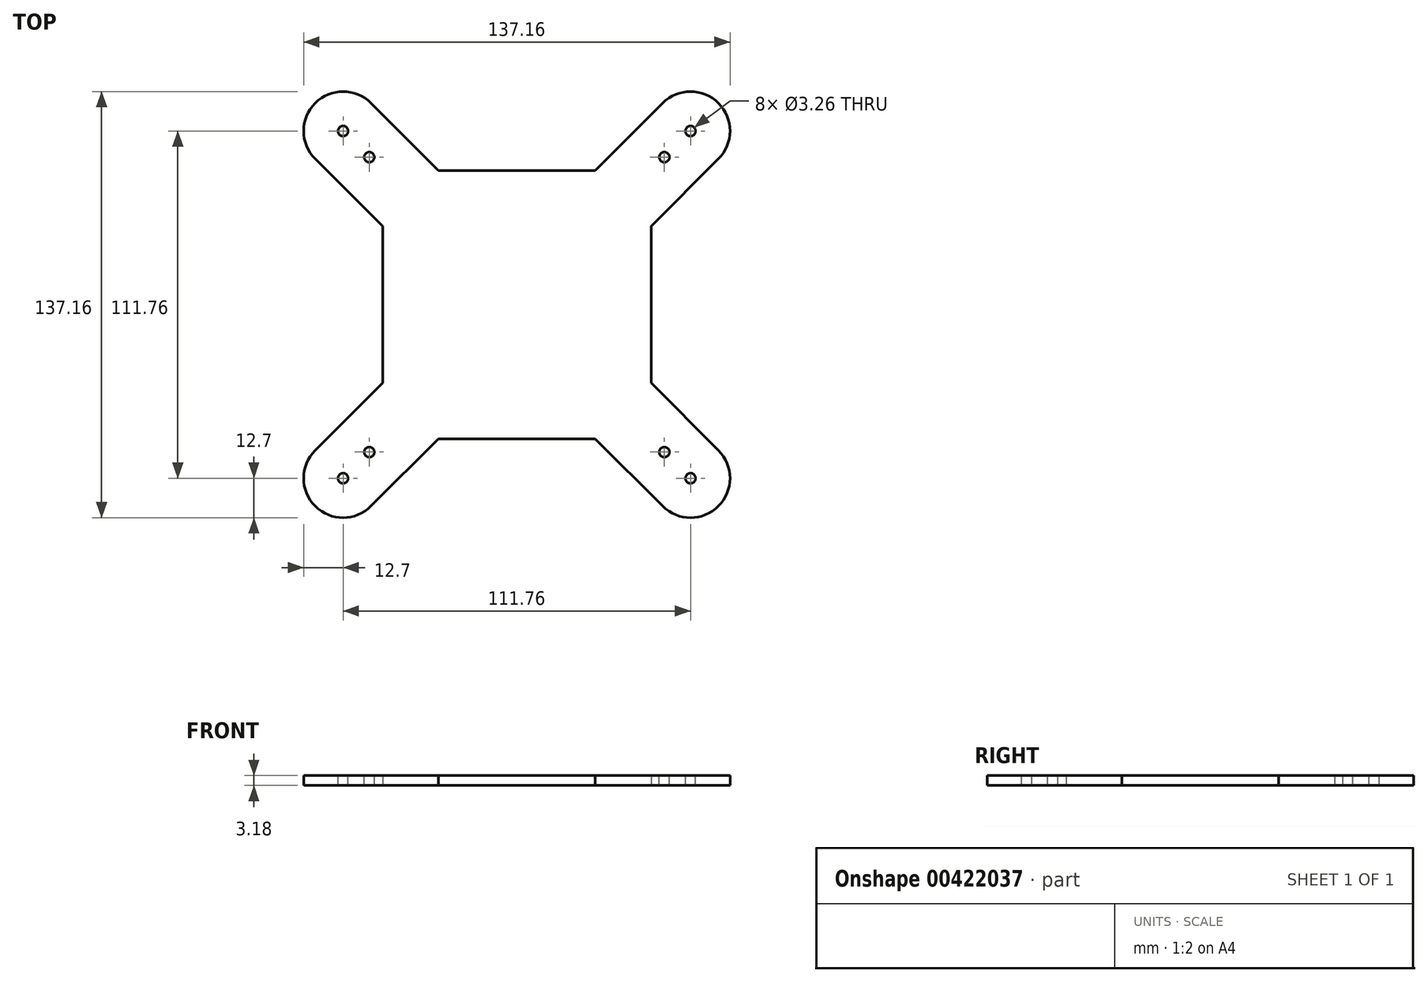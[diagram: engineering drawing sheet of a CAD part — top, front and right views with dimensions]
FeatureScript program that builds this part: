
annotation { "Feature Type Name" : "Feature", "Feature Type Description" : "" }
export const myFeature = defineFeature(function(context is Context, id is Id, definition is map)
    precondition{}
    {
        {
            var Q0;
            Q0=qCreatedBy(makeId("Top.planeOp"),FACE);
            var sketch = newSketch(context, id + "F0", { "sketchPlane" : qUnion([Q0])});
            skPoint(sketch, "E0.middle", {"position": v(0, 0) * mm});
            skArc(sketch, "E1", {"start": v(-46.9, 64.86) * mm, "mid": v(-64.86, 64.86) * mm, "end": v(-64.86, 46.9) * mm});
            skLineSegment(sketch, "E2", {"start": v(0, 0) * mm, "end": v(-55.88, 55.88) * mm, "construction": true});
            skArc(sketch, "E3.1.0", {"start": v(-64.86, -46.9) * mm, "mid": v(-64.86, -64.86) * mm, "end": v(-46.9, -64.86) * mm});
            skArc(sketch, "E3.2.0", {"start": v(46.9, -64.86) * mm, "mid": v(64.86, -64.86) * mm, "end": v(64.86, -46.9) * mm});
            skArc(sketch, "E3.3.0", {"start": v(64.86, 46.9) * mm, "mid": v(64.86, 64.86) * mm, "end": v(46.9, 64.86) * mm});
            skPoint(sketch, "E4", {"position": v(0, 43.18) * mm});
            skLineSegment(sketch, "E5.bottom", {"start": v(25.22, 43.18) * mm, "end": v(-25.22, 43.18) * mm});
            skLineSegment(sketch, "E5.top", {"start": v(25.22, -43.18) * mm, "end": v(-25.22, -43.18) * mm});
            skLineSegment(sketch, "E5.left", {"start": v(43.18, 25.22) * mm, "end": v(43.18, -25.22) * mm});
            skLineSegment(sketch, "E5.right", {"start": v(-43.18, 25.22) * mm, "end": v(-43.18, -25.22) * mm});
            skLineSegment(sketch, "E6", {"start": v(-64.86, 46.9) * mm, "end": v(-43.18, 25.22) * mm});
            skLineSegment(sketch, "E7", {"start": v(-46.9, 64.86) * mm, "end": v(-25.22, 43.18) * mm});
            skLineSegment(sketch, "E8.1.0", {"start": v(46.9, 64.86) * mm, "end": v(25.22, 43.18) * mm});
            skLineSegment(sketch, "E8.1.1", {"start": v(64.86, 46.9) * mm, "end": v(43.18, 25.22) * mm});
            skLineSegment(sketch, "E8.2.0", {"start": v(64.86, -46.9) * mm, "end": v(43.18, -25.22) * mm});
            skLineSegment(sketch, "E8.2.1", {"start": v(46.9, -64.86) * mm, "end": v(25.22, -43.18) * mm});
            skLineSegment(sketch, "E8.3.0", {"start": v(-46.9, -64.86) * mm, "end": v(-25.22, -43.18) * mm});
            skLineSegment(sketch, "E8.3.1", {"start": v(-64.86, -46.9) * mm, "end": v(-43.18, -25.22) * mm});
            skPoint(sketch, "E9.orphan", {"position": v(-43.18, 43.18) * mm});
            skPoint(sketch, "E10.orphan", {"position": v(-43.18, -43.18) * mm});
            skPoint(sketch, "E11.orphan", {"position": v(43.18, -43.18) * mm});
            skPoint(sketch, "E12.orphan", {"position": v(43.18, 43.18) * mm});
            skSolve(sketch);
        }
        {
            var Q0;
            Q0 = qSketchRegion(id + "F0", true);
            extrude(context, id + "F1", {"entities" : qUnion([Q0]), "depth" : 3.17 * mm});
        }
        {
            var Q0;
            Q0=makeQuery(id+"F1.opExtrude","CAP_FACE",FACE,{"disambiguationData":[OSD([sQuery(id+"F0.wireOp",EDGE,"E1"),sQuery(id+"F0.wireOp",EDGE,"E3.1.0"),sQuery(id+"F0.wireOp",EDGE,"E3.2.0"),sQuery(id+"F0.wireOp",EDGE,"E3.3.0"),sQuery(id+"F0.wireOp",EDGE,"E5.bottom"),sQuery(id+"F0.wireOp",EDGE,"E5.top"),sQuery(id+"F0.wireOp",EDGE,"E5.left"),sQuery(id+"F0.wireOp",EDGE,"E5.right"),sQuery(id+"F0.wireOp",EDGE,"E6"),sQuery(id+"F0.wireOp",EDGE,"E7"),sQuery(id+"F0.wireOp",EDGE,"E8.1.0"),sQuery(id+"F0.wireOp",EDGE,"E8.1.1"),sQuery(id+"F0.wireOp",EDGE,"E8.2.0"),sQuery(id+"F0.wireOp",EDGE,"E8.2.1"),sQuery(id+"F0.wireOp",EDGE,"E8.3.0"),sQuery(id+"F0.wireOp",EDGE,"E8.3.1")])],"isStart":false});
            var sketch = newSketch(context, id + "F2", { "sketchPlane" : qUnion([Q0])});
            skPoint(sketch, "E13", {"position": v(-55.88, 55.88) * mm});
            skPoint(sketch, "E14.1.0", {"position": v(-55.88, -55.88) * mm});
            skPoint(sketch, "E14.2.0", {"position": v(55.88, -55.88) * mm});
            skPoint(sketch, "E14.3.0", {"position": v(55.88, 55.88) * mm});
            skPoint(sketch, "E14.center", {"position": v(0, 0) * mm});
            skSolve(sketch);
        }
        {
            var Q0;
            Q0=sQuery(id+"F2.wireOp",VERTEX,"E13");
            var Q1;
            Q1=sQuery(id+"F2.wireOp",VERTEX,"E14.3.0");
            var Q2;
            Q2=sQuery(id+"F2.wireOp",VERTEX,"E14.2.0");
            var Q3;
            Q3=sQuery(id+"F2.wireOp",VERTEX,"E14.1.0");
            var Q4;
            Q4=makeQuery(id+"F1.opExtrude","SWEPT_BODY",BODY,{"disambiguationData":[OSD([sQuery(id+"F0.wireOp",EDGE,"E1"),sQuery(id+"F0.wireOp",EDGE,"E3.1.0"),sQuery(id+"F0.wireOp",EDGE,"E3.2.0"),sQuery(id+"F0.wireOp",EDGE,"E3.3.0"),sQuery(id+"F0.wireOp",EDGE,"E5.bottom"),sQuery(id+"F0.wireOp",EDGE,"E5.top"),sQuery(id+"F0.wireOp",EDGE,"E5.left"),sQuery(id+"F0.wireOp",EDGE,"E5.right"),sQuery(id+"F0.wireOp",EDGE,"E6"),sQuery(id+"F0.wireOp",EDGE,"E7"),sQuery(id+"F0.wireOp",EDGE,"E8.1.0"),sQuery(id+"F0.wireOp",EDGE,"E8.1.1"),sQuery(id+"F0.wireOp",EDGE,"E8.2.0"),sQuery(id+"F0.wireOp",EDGE,"E8.2.1"),sQuery(id+"F0.wireOp",EDGE,"E8.3.0"),sQuery(id+"F0.wireOp",EDGE,"E8.3.1")])]});
            hole(context, id + "F3", {"style" : HoleStyle.SIMPLE, "endStyle" : HoleEndStyle.THROUGH, "standardTappedOrClearance" : lookupTablePath({ "standard" : "ANSI", "fit" : "Normal (ASME)", "size" : "#4", "type" : "Clearance" }), "standardBlindInLast" : lookupTablePath({ "fit" : "Free", "standard" : "ANSI", "size" : "#4", "type" : "Clearance" }), "holeDiameter" : 3.26 * mm, "isTappedThrough" : true, "tappedDepth" : 12.7 * mm, "tapClearance" : 3, "locations" : qUnion([Q0, Q1, Q2, Q3]), "scope" : qUnion([Q4])});
        }
        {
            var Q0;
            Q0=makeQuery(id+"F1.opExtrude","CAP_FACE",FACE,{"disambiguationData":[OSD([sQuery(id+"F0.wireOp",EDGE,"E1"),sQuery(id+"F0.wireOp",EDGE,"E3.1.0"),sQuery(id+"F0.wireOp",EDGE,"E3.2.0"),sQuery(id+"F0.wireOp",EDGE,"E3.3.0"),sQuery(id+"F0.wireOp",EDGE,"E5.bottom"),sQuery(id+"F0.wireOp",EDGE,"E5.top"),sQuery(id+"F0.wireOp",EDGE,"E5.left"),sQuery(id+"F0.wireOp",EDGE,"E5.right"),sQuery(id+"F0.wireOp",EDGE,"E6"),sQuery(id+"F0.wireOp",EDGE,"E7"),sQuery(id+"F0.wireOp",EDGE,"E8.1.0"),sQuery(id+"F0.wireOp",EDGE,"E8.1.1"),sQuery(id+"F0.wireOp",EDGE,"E8.2.0"),sQuery(id+"F0.wireOp",EDGE,"E8.2.1"),sQuery(id+"F0.wireOp",EDGE,"E8.3.0"),sQuery(id+"F0.wireOp",EDGE,"E8.3.1")])],"isStart":false});
            var sketch = newSketch(context, id + "F4", { "sketchPlane" : qUnion([Q0])});
            skCircle(sketch, "E15", {"center": v(-55.88, 55.88) * mm, "radius": 12.7 * mm, "construction": true});
            skLineSegment(sketch, "E16", {"start": v(-55.88, 55.88) * mm, "end": v(-36.94, 36.94) * mm, "construction": true});
            skPoint(sketch, "E17", {"position": v(-47.46, 47.46) * mm});
            skPoint(sketch, "E18", {"position": v(-14.8, 56.02) * mm});
            skPoint(sketch, "E19.1.0", {"position": v(-47.46, -47.46) * mm});
            skPoint(sketch, "E19.2.0", {"position": v(47.46, -47.46) * mm});
            skPoint(sketch, "E19.3.0", {"position": v(47.46, 47.46) * mm});
            skPoint(sketch, "E19.center", {"position": v(0, 0) * mm});
            skSolve(sketch);
        }
        {
            var Q0;
            Q0=sQuery(id+"F4.wireOp",VERTEX,"E17");
            var Q1;
            Q1=sQuery(id+"F4.wireOp",VERTEX,"E19.3.0");
            var Q2;
            Q2=sQuery(id+"F4.wireOp",VERTEX,"E19.2.0");
            var Q3;
            Q3=sQuery(id+"F4.wireOp",VERTEX,"E19.1.0");
            var Q4;
            Q4=makeQuery(id+"F1.opExtrude","SWEPT_BODY",BODY,{"disambiguationData":[OSD([sQuery(id+"F0.wireOp",EDGE,"E1"),sQuery(id+"F0.wireOp",EDGE,"E3.1.0"),sQuery(id+"F0.wireOp",EDGE,"E3.2.0"),sQuery(id+"F0.wireOp",EDGE,"E3.3.0"),sQuery(id+"F0.wireOp",EDGE,"E5.bottom"),sQuery(id+"F0.wireOp",EDGE,"E5.top"),sQuery(id+"F0.wireOp",EDGE,"E5.left"),sQuery(id+"F0.wireOp",EDGE,"E5.right"),sQuery(id+"F0.wireOp",EDGE,"E6"),sQuery(id+"F0.wireOp",EDGE,"E7"),sQuery(id+"F0.wireOp",EDGE,"E8.1.0"),sQuery(id+"F0.wireOp",EDGE,"E8.1.1"),sQuery(id+"F0.wireOp",EDGE,"E8.2.0"),sQuery(id+"F0.wireOp",EDGE,"E8.2.1"),sQuery(id+"F0.wireOp",EDGE,"E8.3.0"),sQuery(id+"F0.wireOp",EDGE,"E8.3.1")])]});
            hole(context, id + "F5", {"style" : HoleStyle.SIMPLE, "endStyle" : HoleEndStyle.THROUGH, "standardTappedOrClearance" : lookupTablePath({ "standard" : "ANSI", "fit" : "Normal (ASME)", "size" : "#4", "type" : "Clearance" }), "standardBlindInLast" : lookupTablePath({ "fit" : "Free", "standard" : "ANSI", "size" : "#4", "type" : "Clearance" }), "holeDiameter" : 3.26 * mm, "isTappedThrough" : true, "tappedDepth" : 12.7 * mm, "tapClearance" : 3, "locations" : qUnion([Q0, Q1, Q2, Q3]), "scope" : qUnion([Q4])});
        }
    });
